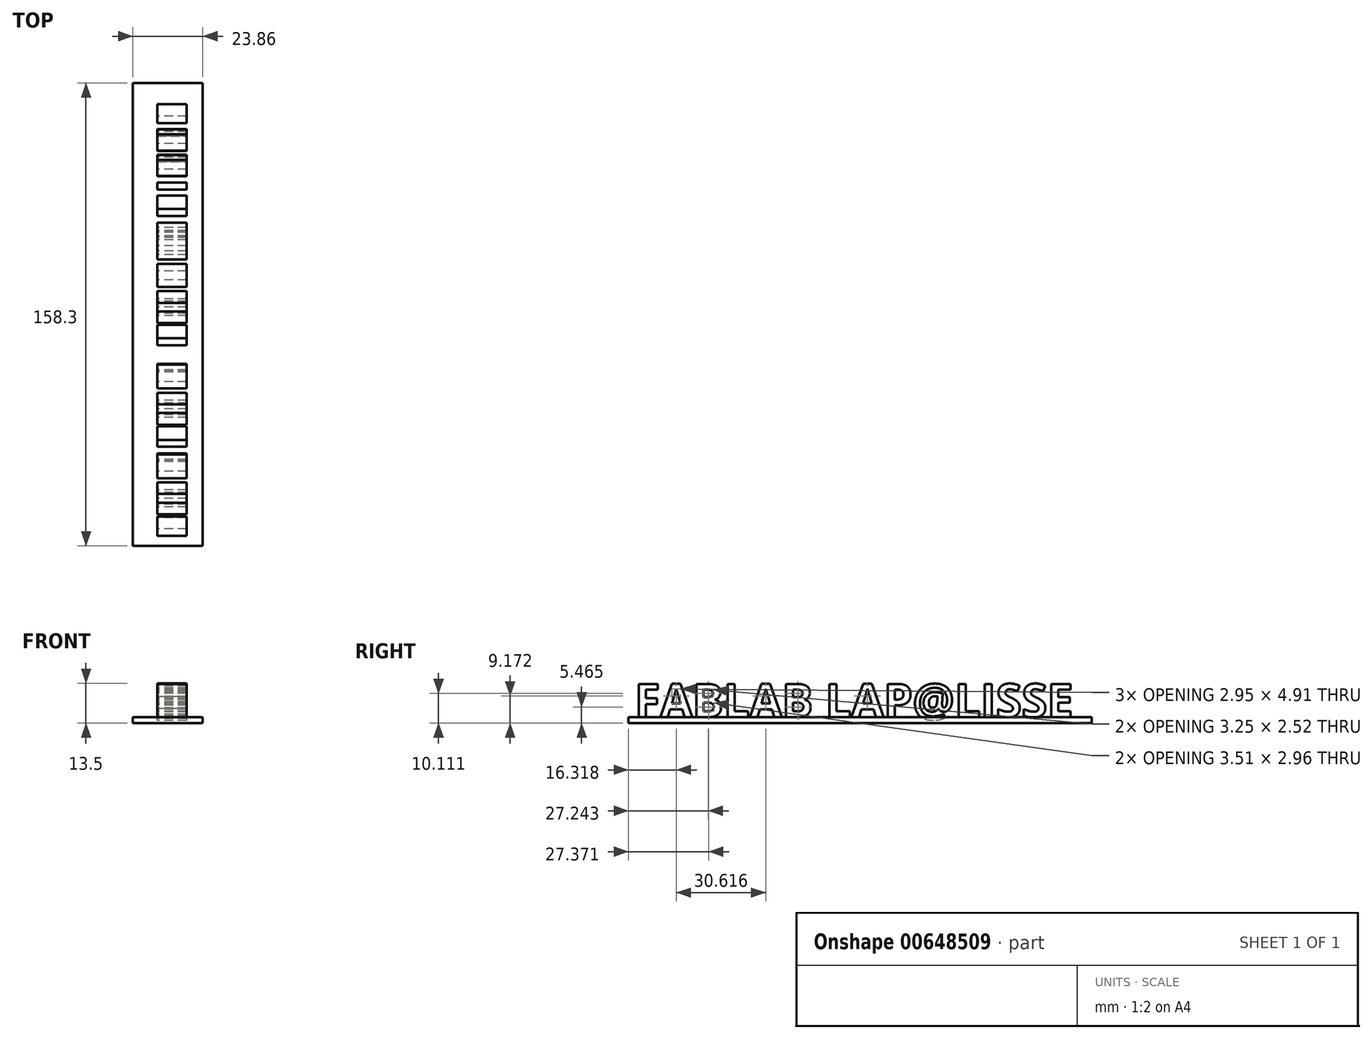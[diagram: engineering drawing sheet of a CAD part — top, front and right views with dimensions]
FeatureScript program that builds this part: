
annotation { "Feature Type Name" : "Feature", "Feature Type Description" : "" }
export const myFeature = defineFeature(function(context is Context, id is Id, definition is map)
    precondition{}
    {
        {
            var Q0;
            Q0=qCreatedBy(makeId("Right.planeOp"),FACE);
            var sketch = newSketch(context, id + "F0", { "sketchPlane" : qUnion([Q0])});
            skText(sketch, "E0", { "text": "FABLAB LAP@LISSE", "fontName": "OpenSans-Bold.ttf"});
            const initialGuessF0  = {"E0": [-0.0122, 0, 1, 0, 0.01144]};
            skSetInitialGuess(sketch, initialGuessF0);
            skSolve(sketch);
        }
        {
            var Q0;
            Q0 = qSketchRegion(id + "F0", true);
            extrude(context, id + "F1", {"entities" : qUnion([Q0]), "depth" : 10 * mm, "offsetDistance" : 25 * mm});
        }
        {
            var Q0;
            Q0=qCreatedBy(makeId("Top.planeOp"),FACE);
            var sketch = newSketch(context, id + "F2", { "sketchPlane" : qUnion([Q0])});
            skLineSegment(sketch, "E1.bottom", {"start": v(-8.37, -14.3) * mm, "end": v(15.5, -14.3) * mm});
            skLineSegment(sketch, "E1.top", {"start": v(-8.37, 144) * mm, "end": v(15.5, 144) * mm});
            skLineSegment(sketch, "E1.left", {"start": v(-8.37, -14.3) * mm, "end": v(-8.37, 144) * mm});
            skLineSegment(sketch, "E1.right", {"start": v(15.5, -14.3) * mm, "end": v(15.5, 144) * mm});
            skSolve(sketch);
        }
        {
            var Q0;
            Q0 = qSketchRegion(id + "F2", true);
            extrude(context, id + "F3", {"entities" : qUnion([Q0]), "oppositeDirection" : true, "depth" : 2 * mm, "offsetDistance" : 25 * mm});
        }
    });
